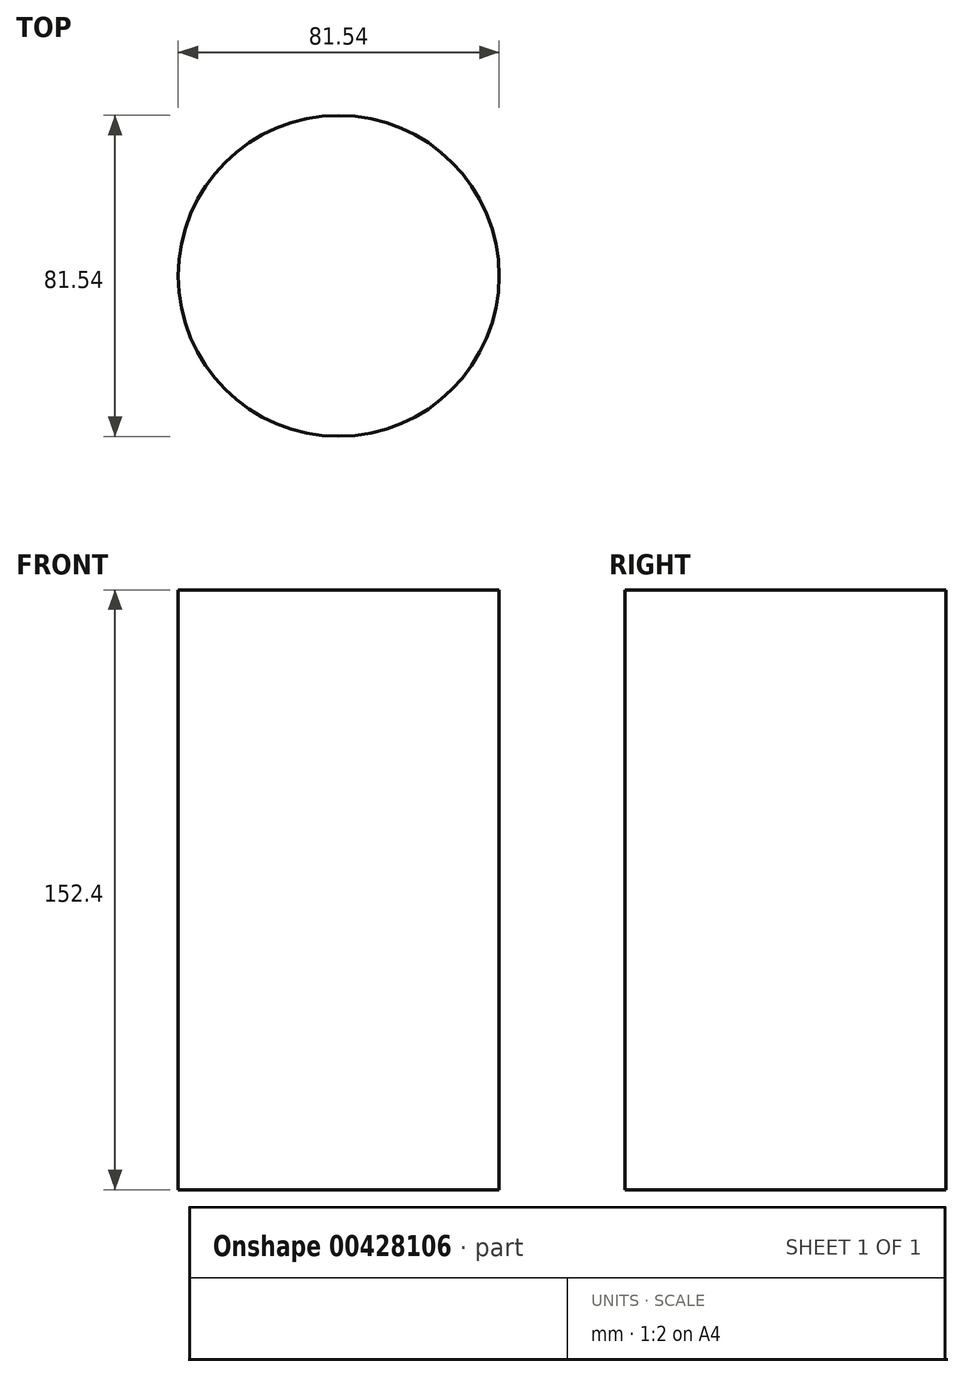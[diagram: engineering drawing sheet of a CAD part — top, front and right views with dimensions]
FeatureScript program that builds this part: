
annotation { "Feature Type Name" : "Feature", "Feature Type Description" : "" }
export const myFeature = defineFeature(function(context is Context, id is Id, definition is map)
    precondition{}
    {
        {
            var Q0;
            Q0=qCreatedBy(makeId("Top.planeOp"),FACE);
            var sketch = newSketch(context, id + "F0", { "sketchPlane" : qUnion([Q0])});
            skCircle(sketch, "E0", {"center": v(0, 0) * mm, "radius": 40.77 * mm});
            skSolve(sketch);
        }
        {
            var Q0;
            Q0=makeQuery(id+"F0.imprint","IMPRINT",FACE,{"disambiguationData":[TD([[makeQuery(id+"F0.imprint","IMPRINT",EDGE,{"derivedFrom":sQuery(id+"F0.wireOp",EDGE,"E0")}),1.0]])]});
            var Q1;
            Q1 = qSketchRegion(id + "FvrGSTmjAVjG6LO_0", true);
            extrude(context, id + "F1", {"entities" : qUnion([Q0, Q1]), "depth" : 152.4 * mm});
        }
    });
